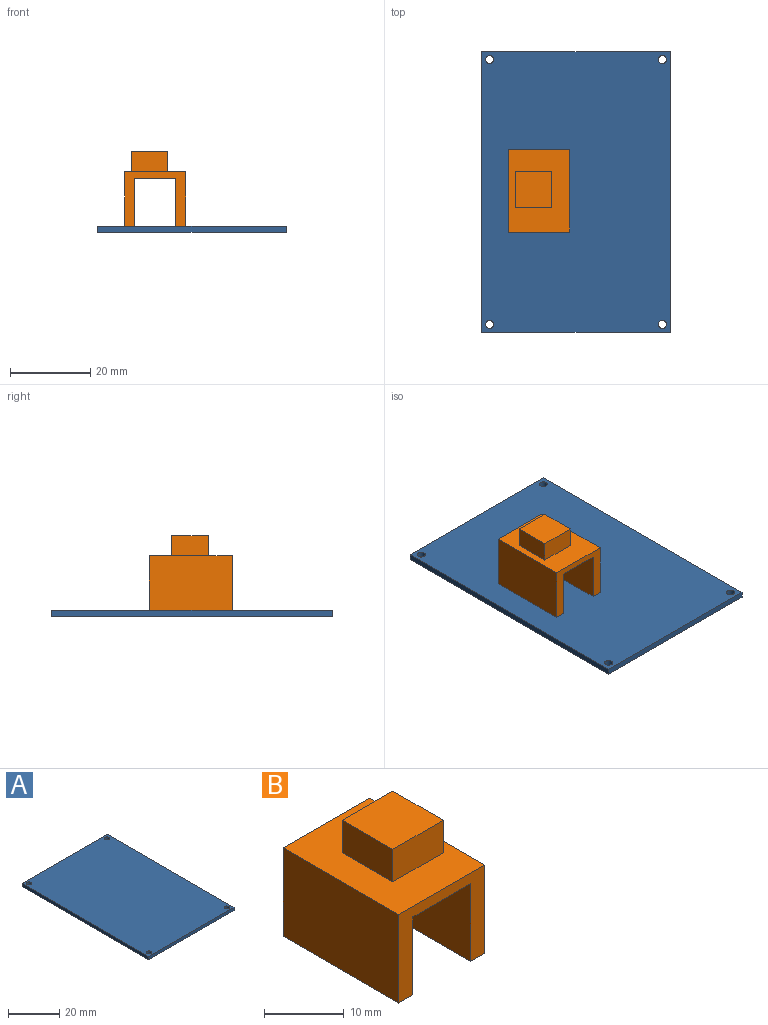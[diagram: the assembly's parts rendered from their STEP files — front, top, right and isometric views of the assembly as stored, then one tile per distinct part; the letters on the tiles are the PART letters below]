
ASSEMBLY  parts=2 mates=1
PART A: 10 faces, bbox 47x70x1.5 mm
  f0: plane 70x1.5mm, normal (-1,0,0), area 105mm2, adj f1,f6,f8,f9
  f1: plane 47x1.5mm, normal (0,-1,0), area 70.5mm2, adj f0,f2,f8,f9
  f2: plane 70x1.5mm, normal (1,0,0), area 105mm2, adj f1,f6,f8,f9
  f3: cylinder r=1mm len=2mm, axis (0,0,-1), area 9.4mm2, adj f8,f9
  f4: cylinder r=1mm len=2mm, axis (0,0,-1), area 9.4mm2, adj f8,f9
  f5: cylinder r=1mm len=2mm, axis (0,0,-1), area 9.4mm2, adj f8,f9
  f6: plane 47x1.5mm, normal (0,1,0), area 70.5mm2, adj f0,f2,f8,f9
  f7: cylinder r=1mm len=2mm, axis (0,0,-1), area 9.4mm2, adj f8,f9
  f8: plane 70x47mm, normal (0,0,1), area 3277.4mm2, adj f0,f1,f2,f3,f4,f5,f6,f7
  f9: plane 70x47mm, normal (0,0,-1), area 3277.4mm2, adj f0,f1,f2,f3,f4,f5,f6,f7
PART B: 15 faces, bbox 15.3x20.6x18.6 mm
  f0: plane 20.6x15.3mm, normal (0,0,1), area 234.2mm2, adj f2,f3,f4,f5,f10,f11,f12,f13
  f1: plane 20.6x10.3mm, normal (0,0,-1), area 212.2mm2, adj f3,f5,f6,f8
  f2: plane 20.6x13.6mm, normal (-1,0,0), area 280.2mm2, adj f0,f3,f5,f9
  f3: plane 15.3x13.6mm, normal (0,-1,0), area 84.5mm2, adj f0,f1,f2,f4,f6,f7,f8,f9
  f4: plane 20.6x13.6mm, normal (1,0,0), area 280.2mm2, adj f0,f3,f5,f7
  f5: plane 15.3x13.6mm, normal (0,1,0), area 84.5mm2, adj f0,f1,f2,f4,f6,f7,f8,f9
  f6: plane 20.6x12mm, normal (-1,0,0), area 247.2mm2, adj f1,f3,f5,f7
  f7: plane 20.6x2.5mm, normal (0,0,-1), area 51.5mm2, adj f3,f4,f5,f6
  f8: plane 20.6x12mm, normal (1,0,0), area 247.2mm2, adj f1,f3,f5,f9
  f9: plane 20.6x2.5mm, normal (0,0,-1), area 51.5mm2, adj f2,f3,f5,f8
  f10: plane 9x5mm, normal (0,1,0), area 45mm2, adj f0,f11,f13,f14
  f11: plane 9x5mm, normal (-1,0,0), area 45mm2, adj f0,f10,f12,f14
  f12: plane 9x5mm, normal (0,-1,0), area 45mm2, adj f0,f11,f13,f14
  f13: plane 9x5mm, normal (1,0,0), area 45mm2, adj f0,f10,f12,f14
  f14: plane 9x9mm, normal (0,0,1), area 81mm2, adj f10,f11,f12,f13
PLACE A t=(8.2,-10.55,15.83)mm fixed
PLACE B rot(axis=(0,0,1),180deg) t=(30.2,35.05,29.33)mm
MATE fastened A.f8 <-> B.f7  axis (0,0,1) through (8.2,-10.55,17.33)mm
